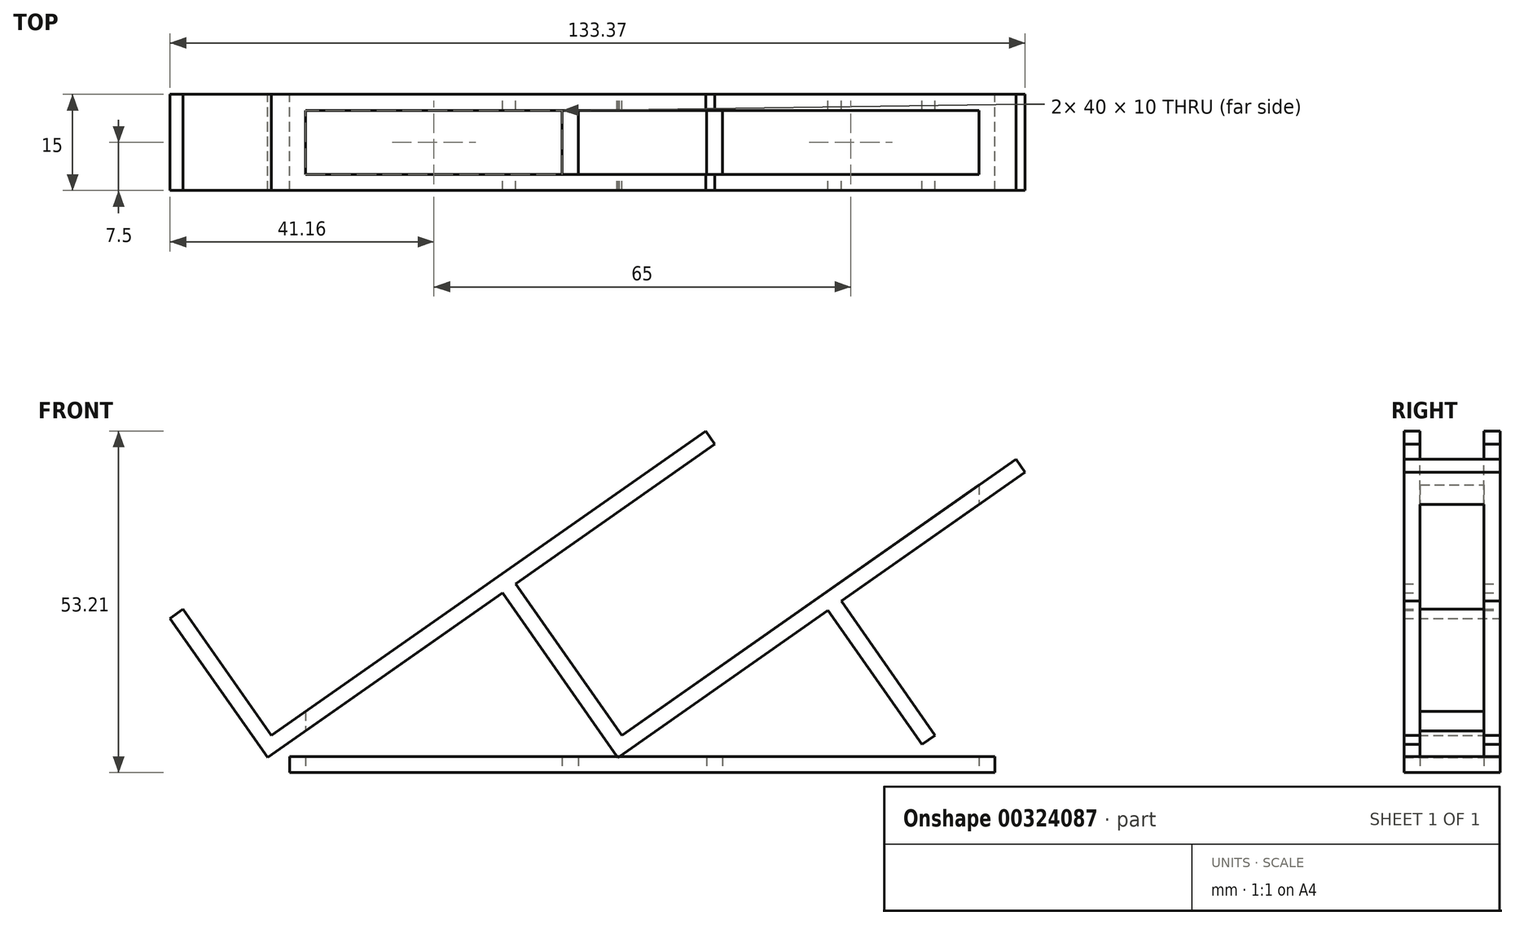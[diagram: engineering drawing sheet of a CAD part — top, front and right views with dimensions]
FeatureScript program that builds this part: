
annotation { "Feature Type Name" : "Feature", "Feature Type Description" : "" }
export const myFeature = defineFeature(function(context is Context, id is Id, definition is map)
    precondition{}
    {
        {
            var Q0;
            Q0=qCreatedBy(makeId("Front.planeOp"),FACE);
            var sketch = newSketch(context, id + "F0", { "sketchPlane" : qUnion([Q0])});
            skLineSegment(sketch, "E0.bottom", {"start": v(-55, 0) * mm, "end": v(55, 0) * mm});
            skLineSegment(sketch, "E0.top", {"start": v(-55, 2.5) * mm, "end": v(55, 2.5) * mm});
            skLineSegment(sketch, "E0.left", {"start": v(-55, 0) * mm, "end": v(-55, 2.5) * mm});
            skLineSegment(sketch, "E0.right", {"start": v(55, 0) * mm, "end": v(55, 2.5) * mm});
            skLineSegment(sketch, "E1", {"start": v(-52.5, 0) * mm, "end": v(-52.5, 2.5) * mm});
            skLineSegment(sketch, "E2", {"start": v(52.5, 0) * mm, "end": v(52.5, 2.5) * mm});
            skLineSegment(sketch, "E3", {"start": v(-69.34, 30.48) * mm, "end": v(3.57, 81.53) * mm});
            skLineSegment(sketch, "E4", {"start": v(3.57, 81.53) * mm, "end": v(17.9, 61.05) * mm});
            skLineSegment(sketch, "E5", {"start": v(17.9, 61.05) * mm, "end": v(-55, 10) * mm});
            skLineSegment(sketch, "E6", {"start": v(-55, 10) * mm, "end": v(-69.34, 30.48) * mm});
            skLineSegment(sketch, "E7", {"start": v(-12.84, 30.98) * mm, "end": v(60.07, 82.03) * mm});
            skLineSegment(sketch, "E8", {"start": v(60.07, 82.03) * mm, "end": v(74.4, 61.55) * mm});
            skLineSegment(sketch, "E9", {"start": v(74.4, 61.55) * mm, "end": v(1.5, 10.5) * mm});
            skLineSegment(sketch, "E10", {"start": v(1.5, 10.5) * mm, "end": v(-12.84, 30.98) * mm});
            skPoint(sketch, "E11.orphan", {"position": v(-9.92, 2.5) * mm});
            skLineSegment(sketch, "E12", {"start": v(-71.61, 25.46) * mm, "end": v(-57.85, 5.8) * mm});
            skLineSegment(sketch, "E13", {"start": v(-57.85, 5.8) * mm, "end": v(-21.18, 31.47) * mm});
            skLineSegment(sketch, "E14", {"start": v(-21.18, 31.47) * mm, "end": v(-3.2, 5.8) * mm});
            skLineSegment(sketch, "E15", {"start": v(-3.2, 5.8) * mm, "end": v(29.59, 28.76) * mm});
            skLineSegment(sketch, "E16", {"start": v(29.59, 28.76) * mm, "end": v(45.67, 5.8) * mm});
            skLineSegment(sketch, "E17", {"start": v(45.67, 5.8) * mm, "end": v(43.62, 4.36) * mm});
            skLineSegment(sketch, "E18", {"start": v(43.62, 4.36) * mm, "end": v(28.98, 25.28) * mm});
            skLineSegment(sketch, "E19", {"start": v(28.98, 25.28) * mm, "end": v(-3.82, 2.32) * mm});
            skLineSegment(sketch, "E20", {"start": v(-3.82, 2.32) * mm, "end": v(-21.8, 27.99) * mm});
            skLineSegment(sketch, "E21", {"start": v(-21.8, 27.99) * mm, "end": v(-58.46, 2.32) * mm});
            skLineSegment(sketch, "E22", {"start": v(-58.46, 2.32) * mm, "end": v(-73.66, 24.02) * mm});
            skLineSegment(sketch, "E23", {"start": v(-73.66, 24.02) * mm, "end": v(-71.61, 25.46) * mm});
            skLineSegment(sketch, "E24", {"start": v(-22.95, 30.23) * mm, "end": v(9.87, 53.21) * mm});
            skLineSegment(sketch, "E25", {"start": v(9.87, 53.21) * mm, "end": v(11.3, 51.17) * mm});
            skLineSegment(sketch, "E26", {"start": v(11.3, 51.17) * mm, "end": v(-28.1, 23.58) * mm});
            skLineSegment(sketch, "E27", {"start": v(25.1, 25.62) * mm, "end": v(58.28, 48.85) * mm});
            skLineSegment(sketch, "E28", {"start": v(58.28, 48.85) * mm, "end": v(59.7, 46.8) * mm});
            skLineSegment(sketch, "E29", {"start": v(59.7, 46.8) * mm, "end": v(23.64, 21.54) * mm});
            skSolve(sketch);
        }
        {
            var Q0;
            Q0=makeQuery(id+"F0.imprint","IMPRINT",FACE,{"disambiguationData":[TD([[makeQuery(id+"F0.imprint","IMPRINT",EDGE,{"derivedFrom":sQuery(id+"F0.wireOp",EDGE,"E12")}),-1.0]])]});
            var Q1;
            {var subQ5=sQuery(id+"F0.wireOp",EDGE,"E25");Q1=makeQuery(id+"F0.imprint","IMPRINT",FACE,{"disambiguationData":[TD([[makeQuery(id+"F0.imprint","IMPRINT",EDGE,{"derivedFrom":subQ5}),-1.0]])]});}
            var Q2;
            {var subQ0=sQuery(id+"F0.wireOp",EDGE,"E15");Q2=makeQuery(id+"F0.imprint","IMPRINT",FACE,{"disambiguationData":[TD([[makeQuery(id+"F0.imprint","IMPRINT",EDGE,{"derivedFrom":subQ0}),-1.0]])]});}
            var Q3;
            {var subQ0=sQuery(id+"F0.wireOp",EDGE,"E17");Q3=makeQuery(id+"F0.imprint","IMPRINT",FACE,{"disambiguationData":[TD([[makeQuery(id+"F0.imprint","IMPRINT",EDGE,{"derivedFrom":subQ0}),-1.0]])]});}
            var Q4;
            {var subQ5=sQuery(id+"F0.wireOp",EDGE,"E28");Q4=makeQuery(id+"F0.imprint","IMPRINT",FACE,{"disambiguationData":[TD([[makeQuery(id+"F0.imprint","IMPRINT",EDGE,{"derivedFrom":subQ5}),-1.0]])]});}
            var Q5;
            {var subQ0=sQuery(id+"F0.wireOp",EDGE,"E1");Q5=makeQuery(id+"F0.imprint","IMPRINT",FACE,{"disambiguationData":[TD([[makeQuery(id+"F0.imprint","IMPRINT",EDGE,{"derivedFrom":subQ0}),-1.0]])]});}
            var Q6;
            {var subQ0=sQuery(id+"F0.wireOp",EDGE,"E0.right");Q6=makeQuery(id+"F0.imprint","IMPRINT",FACE,{"disambiguationData":[TD([[makeQuery(id+"F0.imprint","IMPRINT",EDGE,{"derivedFrom":subQ0}),1.0]])]});}
            var Q7;
            {var subQ0=sQuery(id+"F0.wireOp",EDGE,"E0.left");Q7=makeQuery(id+"F0.imprint","IMPRINT",FACE,{"disambiguationData":[TD([[makeQuery(id+"F0.imprint","IMPRINT",EDGE,{"derivedFrom":subQ0}),-1.0]])]});}
            extrude(context, id + "F1", {"entities" : qUnion([Q0, Q1, Q2, Q3, Q4, Q5, Q6, Q7]), "depth" : 15 * mm, "offsetDistance" : 25 * mm});
        }
        {
            var Q0;
            Q0=qCreatedBy(makeId("Top.planeOp"),FACE);
            var sketch = newSketch(context, id + "F2", { "sketchPlane" : qUnion([Q0])});
            skLineSegment(sketch, "E30.bottom", {"start": v(-52.5, -2.5) * mm, "end": v(-12.5, -2.5) * mm});
            skLineSegment(sketch, "E30.top", {"start": v(-52.5, -12.5) * mm, "end": v(-12.5, -12.5) * mm});
            skLineSegment(sketch, "E30.left", {"start": v(-52.5, -2.5) * mm, "end": v(-52.5, -12.5) * mm});
            skLineSegment(sketch, "E30.right", {"start": v(-12.5, -2.5) * mm, "end": v(-12.5, -12.5) * mm});
            skLineSegment(sketch, "E31.bottom", {"start": v(-10, -2.5) * mm, "end": v(10, -2.5) * mm});
            skLineSegment(sketch, "E31.top", {"start": v(-10, -12.5) * mm, "end": v(10, -12.5) * mm});
            skLineSegment(sketch, "E31.left", {"start": v(-10, -2.5) * mm, "end": v(-10, -12.5) * mm});
            skLineSegment(sketch, "E31.right", {"start": v(10, -2.5) * mm, "end": v(10, -12.5) * mm});
            skLineSegment(sketch, "E32.bottom", {"start": v(12.5, -2.5) * mm, "end": v(52.5, -2.5) * mm});
            skLineSegment(sketch, "E32.top", {"start": v(12.5, -12.5) * mm, "end": v(52.5, -12.5) * mm});
            skLineSegment(sketch, "E32.left", {"start": v(12.5, -2.5) * mm, "end": v(12.5, -12.5) * mm});
            skLineSegment(sketch, "E32.right", {"start": v(52.5, -2.5) * mm, "end": v(52.5, -12.5) * mm});
            skSolve(sketch);
        }
        {
            var Q0;
            Q0=makeQuery(id+"F2.imprint","IMPRINT",FACE,{"disambiguationData":[TD([[makeQuery(id+"F2.imprint","IMPRINT",EDGE,{"derivedFrom":sQuery(id+"F2.wireOp",EDGE,"E31.bottom")}),-1.0]])]});
            var Q1;
            Q1=makeQuery(id+"F2.imprint","IMPRINT",FACE,{"disambiguationData":[TD([[makeQuery(id+"F2.imprint","IMPRINT",EDGE,{"derivedFrom":sQuery(id+"F2.wireOp",EDGE,"E32.bottom")}),-1.0]])]});
            var Q2;
            Q2=makeQuery(id+"F2.imprint","IMPRINT",FACE,{"disambiguationData":[TD([[makeQuery(id+"F2.imprint","IMPRINT",EDGE,{"derivedFrom":sQuery(id+"F2.wireOp",EDGE,"E30.bottom")}),-1.0]])]});
            extrude(context, id + "F3", {"entities" : qUnion([Q0, Q1, Q2]), "operationType" : NewBodyOperationType.REMOVE, "depth" : 70 * mm, "offsetDistance" : 25 * mm});
        }
        {
            var Q0;
            Q0=qCreatedBy(makeId("Right.planeOp"),FACE);
            var sketch = newSketch(context, id + "F4", { "sketchPlane" : qUnion([Q0])});
            skLineSegment(sketch, "E33.bottom", {"start": v(-2.5, 2.5) * mm, "end": v(-12.5, 2.5) * mm});
            skLineSegment(sketch, "E33.top", {"start": v(-2.5, 62.5) * mm, "end": v(-12.5, 62.5) * mm});
            skLineSegment(sketch, "E33.left", {"start": v(-2.5, 2.5) * mm, "end": v(-2.5, 62.5) * mm});
            skLineSegment(sketch, "E33.right", {"start": v(-12.5, 2.5) * mm, "end": v(-12.5, 62.5) * mm});
            skSolve(sketch);
        }
        {
            var Q0;
            Q0=makeQuery(id+"F4.imprint","IMPRINT",FACE,{"disambiguationData":[TD([[makeQuery(id+"F4.imprint","IMPRINT",EDGE,{"derivedFrom":sQuery(id+"F4.wireOp",EDGE,"E33.bottom")}),-1.0]])]});
            extrude(context, id + "F5", {"entities" : qUnion([Q0]), "operationType" : NewBodyOperationType.REMOVE, "oppositeDirection" : true, "depth" : 25 * mm, "offsetDistance" : 25 * mm, "hasSecondDirection" : true, "secondDirectionOppositeDirection" : false, "secondDirectionDepth" : 25 * mm});
        }
    });
